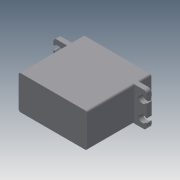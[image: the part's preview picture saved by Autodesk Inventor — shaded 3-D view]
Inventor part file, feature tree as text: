
AUTODESK INVENTOR PART (.ipt)
format: ipt  version: 2013 (Build 170138000, 138)  size: 192,000 bytes
history: native  units: mm
features: fillet x12, extrude x8, sketch x8, chamfer x1
ambient origin geometry x8: Origin, YZ Plane, XZ Plane, XY Plane, X Axis, Y Axis, Z Axis, Center Point
bodies: Solid1 (feature_tree)
feature tree (29):
  extrude  "Extrusion1"  Depth=7.4mm TaperAngle=0.0deg
  sketch  "Sketch2"  dims[d10=7.4mm d11=0.0mm d18=5.8mm d19=0.0mm]
  extrude  "Extrusion2"  Depth=5.8mm TaperAngle=0.0deg
  extrude  "Extrusion3"  Depth=4.0mm TaperAngle=0.0deg
  extrude  "Extrusion4"  Depth=2.0mm
  extrude  "Extrusion5"  Depth=2.0mm
  fillet  "Fillet1"  Radius=1.0mm
  fillet  "Fillet2"  Radius=1.0mm
  fillet  "Fillet3"  Radius=1.0mm
  fillet  "Fillet4"  Radius=1.0mm
  fillet  "Fillet5"  Radius=1.0mm
  fillet  "Fillet6"  Radius=1.0mm
  fillet  "Fillet7"  Radius=1.0mm
  fillet  "Fillet8"  Radius=1.0mm
  fillet  "Fillet9"  Radius=4.0mm
  fillet  "Fillet10"  Radius=3.0mm
  fillet  "Fillet11"  Radius=3.0mm
  fillet  "Fillet12"  [1 undecoded]
  extrude  "Extrusion6"  [1 undecoded]
  chamfer  "Chamfer3"  [1 undecoded]
  sketch  "Sketch7"
  sketch  "Sketch8"
  extrude  "Extrusion7"  [1 undecoded]
  extrude  "Extrusion8"  [1 undecoded]
  sketch  "Sketch1"  dims[d2=43.7mm d3=0.0mm d8=7.4mm d9=0.0mm]
  sketch  "Sketch3"  dims[d20=5.0mm d21=4.0mm d22=0.0mm]
  sketch  "Sketch4"  dims[d26=2.0mm d27=2.0mm]
  sketch  "Sketch5"  dims[d28=2.0mm d29=2.0mm d30=1.0mm d31=1.0mm d32=1.0mm d33=1.0mm d34=1.0mm d35=1.0mm d36=1.0mm d37=1.0mm d39=4.0mm d40=0.0mm]
  sketch  "Sketch6"  dims[d44=1.8mm d45=1.6mm d46=45.0deg d71=3.0mm d72=0.0mm d73=3.0mm d74=0.0mm]
note: 5 required parameter values undecoded (feature->parameter linkage not recoverable at this tier; creation-order binding heuristic only, values carry confidence <= 0.55)
